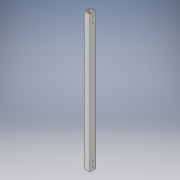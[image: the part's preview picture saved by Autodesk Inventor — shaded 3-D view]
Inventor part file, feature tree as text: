
AUTODESK INVENTOR PART (.ipt)
format: ipt  version: 2018 (Build 220112000, 112)  size: 122,368 bytes
history: native  units: in
note: dims shown in document units (in); Inventor stores cm internally (conversion verified against a paired STEP export)
features: extrude x2, sketch x2
ambient origin geometry x8: Origin, YZ Plane, XZ Plane, XY Plane, X Axis, Y Axis, Z Axis, Center Point
bodies: Solid1 (feature_tree)
feature tree (4):
  extrude  "Extrusion1"  Depth=1.0in
  extrude  "Extrusion2"  Depth=24.0in TaperAngle=0.0deg
  sketch  "Sketch1"  dims[d0=1.0in d1=1.0in]
  sketch  "Sketch2"  dims[d2=0.125in d3=24.0in d4=0.0in d5=0.5in d6=1.0in d7=0.5in d8=1.0in d9=0.2031in d10=0.2031in d11=0.2031in d12=0.2031in d13=25.0in d14=0.0in]
